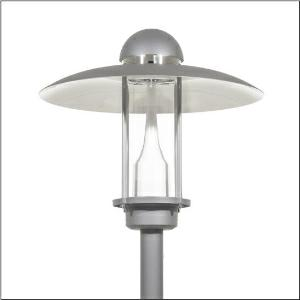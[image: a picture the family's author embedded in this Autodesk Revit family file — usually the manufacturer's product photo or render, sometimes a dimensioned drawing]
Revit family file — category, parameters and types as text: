
# Revit family: city-light_elegance_iq___p1_0a_5xa5265nf14h_5982
name_source: partatom
category: Lighting Fixtures
units: mm (PartAtom-declared; Revit-internal decimal feet)

## family parameters
Cut with Voids When Loaded = No
Host = Face
Light Source = No
Part Type = Normal
Room Calculation Point = No
Round Connector Dimension = Use Diameter
Shared = No

## types (1)
- --- (1 x LED, 1440 lm, 11.8 W, 2700K)
    Apparent Load = 12 VA
    CIE Flux Codes = 32 62 91 97 100
    Color Rendering = 70
    Color Temperature = 2700K
    Default Elevation = 1800 mm
    Description = City-Light Elegance iQ, mast luminaire, Module 540 iQ-SR, primary light control with 3 zone facetted reflector, of plastic, silver coated, highly specular, structured, primary optical cover: cover, of PMMA, transparent, light distribution: P1.0a, light emission: direct distribution, primary light characteristic: strongly asymmetric, installation type: post-top, LED, High Power LED, rated luminous flux: 1.440lm, luminous efficacy: 122lm/W, light colour: 727, colour temperature: 2700K, control gear: ECG iQ, control: presetting dimming logarithmic, Street-Remote, Auto-Match, Temp-Guard, Lumen-Switch, Night-Set, Smart-Wire, Light-Fading, Desk-Remote (wireless, voltage-free reading and setting of iQ features in the workshop via application-optimized NFC function/RFID function), optimised constant luminous flux control (CLO 2.0), with terminal, 6-pole, max. 2.5mm², mains connection: 230..240V, AC, 50/60Hz, start of lifetime: 12W, end of service life: 12W, reduction: 6W, luminaire housing, upper part, of aluminium, coated, Siteco® metallic grey (DB 702S), diameter: 750mm, height: 675mm, spigot size: d x l = 76 x 70mm (post-top) | with reducer (optional accessory) 60 x 70mm, post-top mast mounting element, of diecast aluminium, coated, Siteco® metallic grey (DB 702S), Module 540 iQ-SR, traffic white (RAL 9016), equipment: standard, protection rating (complete): IP65, insulation class (complete): insulation class II (safety insulation), certification: CE, ENEC, VDE, packaging unit: 1 piece

Light Distribution: P1.0a
    Height = 675 mm
    Lamp = 1 x LED
    Lamp Light Flux = 1440 lm
    Lamp Power = 11.8 W
    Lamp count = 1
    Length = 750 mm
    Luminous efficacy = 122 lm/W
    Manufacturer = Siteco
    ModVariant = No
    Model = 5XA5265NF14H
    Number of Poles = 1
    OnlyDefault = Yes
    Power Factor = 1
    Product Name = City-Light Elegance iQ | P1.0a
    Product group = mast luminaire | pylon top
    ProductGroupID = 6100
    Protection Class = Protection class II
    Protection Degree = IP 65
    RLX_Detail_Level = 1
    RLX_Emergency_Light_Flux = 0 lm
    RLX_Emergency_Type = 0
    RLX_Emergency_Type_DB = No
    RlxData = <blob elided: 101913 chars, md5=e615fa7b>
    Socket = socket
    Standby Power = 0 W
    System Light Flux = 1440 lm
    System Power = 12 W
    Type Comments = factory setting: luminous flux: 100 % | dim-lin: 254 | 472 mA
    Type Image = l_1006912.jpg
    URL = http://relux.com
    VarID = @adj_085519
    Voltage = 0 V
    Weight = 0.00 kg
    Width = 0 mm  [stored 0 ft]

note: [stored X ft] marks values corroborated as IEEE doubles in the binary element streams (Revit-internal decimal feet)

## geometry (parser evidence)
native form markers: Blend x4, Sweep x10
no freeform markers — native parametric forms only
